# Revit family: UTB
name_source: partatom
category: Lighting Fixtures
revit_build: Autodesk Revit Architecture 2012 (Build: 20110309_2315(x64)
units: mm (PartAtom-declared; Revit-internal decimal feet)

## types (8) — shared parameters
Apparent Load = 25 VA
Bracket material = Paint - Hubbell -  Black
Color Filter = 16777215
Connector Description = Lighting Connector
Default Elevation = 48 "
Description = Utilibay™ LED Highbay
Dimming Lamp Color Temperature Shift = <None>
Emit Shape Visible in Rendering = No
Emit from Circle Diameter = 12 "
Lamp = LED
Load Classification = Lighting
Manufacturer = Hubbell Industrial Lighting
Manufacturer Fax = 866-898-0131
Model = UTB
Photometric Notes = Download Photometric web link
Photometric Web Link = http://www.hubbellindustrial.com
Product Documentation Link = http://www.hubbellindustrial.com
Product Material = Paint - Hubbell - Aluminium Grey
Product Page URL = http://www.hubbellindustrial.com
Reflector Finish = Glass - Hubbell - White
Tilt Angle = -90.00°
URL = http://www.hubbellindustrial.com
Watt = 255 W
Wattage Comments = 255 W/ 167 W

## per-type parameters (varying)
| type | Photometric Web File |
| UTB-4K-SB16-HO-CDL | UTB-4K-SB16-HO-CDL.IES |
| UTB-4K-SB16-HO-DLR | UTB-4K-SB16-HO-DLR.IES |
| UTB-4K-SB16-HO-N | UTB-4K-SB16-HO-N.IES |
| UTB-4K-SB16-HO-P95 | UTB-4K-SB16-MO-CDL.IES |
| UTB-4K-SB16-MO-CDL | UTB-4K-SB16-MO-CDL.IES |
| UTB-4K-SB16-MO-DLR | UTB-4K-SB16-MO-DLR.IES |
| UTB-4K-SB16-MO-N | UTB-4K-SB16-MO-N.IES |
| UTB-4K-SB16-MO-P95 | UTB-4K-SB16-MO-P95.IES |

## geometry (parser evidence)
native form markers: Blend x1, Sweep x4
no freeform markers — native parametric forms only
